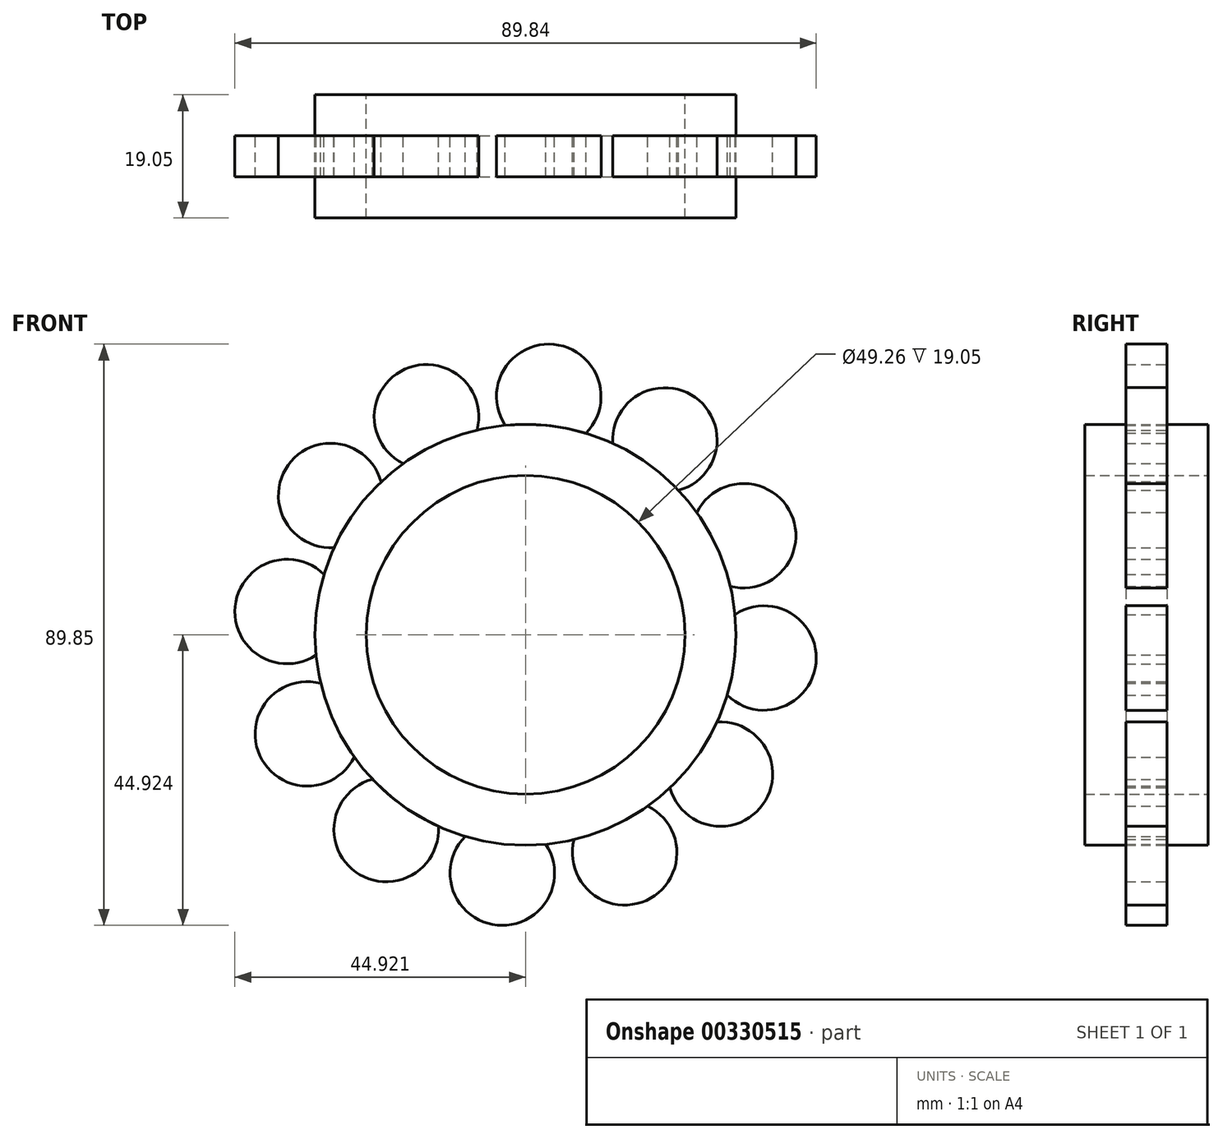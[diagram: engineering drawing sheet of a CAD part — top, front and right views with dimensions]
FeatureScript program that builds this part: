
annotation { "Feature Type Name" : "Feature", "Feature Type Description" : "" }
export const myFeature = defineFeature(function(context is Context, id is Id, definition is map)
    precondition{}
    {
        {
            var Q0;
            Q0=qCreatedBy(makeId("Front.planeOp"),FACE);
            var sketch = newSketch(context, id + "F0", { "sketchPlane" : qUnion([Q0])});
            skCircle(sketch, "E0", {"center": v(-26.17, 22.7) * mm, "radius": 32.53 * mm});
            skSolve(sketch);
        }
        {
            var Q0;
            Q0=sQuery(id+"F0.wireOp",EDGE,"E0");
            extrude(context, id + "F1", {"bodyType" : ToolBodyType.SURFACE, "surfaceEntities" : qUnion([Q0]), "depth" : 6.35 * mm});
        }
        {
            var Q0;
            Q0=qCreatedBy(makeId("Front.planeOp"),FACE);
            var sketch = newSketch(context, id + "F2", { "sketchPlane" : qUnion([Q0])});
            skArc(sketch, "E1", {"start": v(-57.82, 15.2) * mm, "mid": v(-67.23, 4.05) * mm, "end": v(-52.64, 3.8) * mm});
            skCircle(sketch, "E2.0", {"center": v(-26.17, 22.7) * mm, "radius": 32.53 * mm});
            skArc(sketch, "E3.1.0", {"start": v(-49.83, 0.38) * mm, "mid": v(-52.4, -13.98) * mm, "end": v(-39.65, -6.9) * mm});
            skArc(sketch, "E3.2.0", {"start": v(-35.5, -8.46) * mm, "mid": v(-30.54, -22.18) * mm, "end": v(-23.04, -9.67) * mm});
            skArc(sketch, "E3.3.0", {"start": v(-18.66, -8.95) * mm, "mid": v(-7.51, -18.36) * mm, "end": v(-7.27, -3.77) * mm});
            skArc(sketch, "E3.4.0", {"start": v(-3.84, -0.95) * mm, "mid": v(10.52, -3.53) * mm, "end": v(3.44, 9.23) * mm});
            skArc(sketch, "E3.5.0", {"start": v(5, 13.38) * mm, "mid": v(18.72, 18.33) * mm, "end": v(6.2, 25.84) * mm});
            skArc(sketch, "E3.6.0", {"start": v(5.48, 30.21) * mm, "mid": v(14.9, 41.36) * mm, "end": v(0.3, 41.6) * mm});
            skArc(sketch, "E3.7.0", {"start": v(-2.51, 45.03) * mm, "mid": v(0.06, 59.39) * mm, "end": v(-12.7, 52.3) * mm});
            skArc(sketch, "E3.8.0", {"start": v(-16.85, 53.87) * mm, "mid": v(-21.8, 67.59) * mm, "end": v(-29.3, 55.08) * mm});
            skArc(sketch, "E3.9.0", {"start": v(-33.68, 54.35) * mm, "mid": v(-44.82, 63.76) * mm, "end": v(-45.07, 49.18) * mm});
            skArc(sketch, "E3.10.0", {"start": v(-48.5, 46.36) * mm, "mid": v(-62.85, 48.93) * mm, "end": v(-55.77, 36.18) * mm});
            skArc(sketch, "E3.11.0", {"start": v(-57.33, 32.03) * mm, "mid": v(-71.05, 27.08) * mm, "end": v(-58.55, 19.57) * mm});
            skSolve(sketch);
        }
        {
            var Q0;
            {var subQ0=sQuery(id+"F2.wireOp",EDGE,"E3.11.0");Q0=makeQuery(id+"F2.imprint","IMPRINT",FACE,{"disambiguationData":[TD([[makeQuery(id+"F2.imprint","IMPRINT",EDGE,{"derivedFrom":subQ0}),1.0]])]});}
            var Q1;
            {var subQ0=sQuery(id+"F2.wireOp",EDGE,"E3.10.0");Q1=makeQuery(id+"F2.imprint","IMPRINT",FACE,{"disambiguationData":[TD([[makeQuery(id+"F2.imprint","IMPRINT",EDGE,{"derivedFrom":subQ0}),1.0]])]});}
            var Q2;
            {var subQ0=sQuery(id+"F2.wireOp",EDGE,"E3.9.0");Q2=makeQuery(id+"F2.imprint","IMPRINT",FACE,{"disambiguationData":[TD([[makeQuery(id+"F2.imprint","IMPRINT",EDGE,{"derivedFrom":subQ0}),1.0]])]});}
            var Q3;
            {var subQ0=sQuery(id+"F2.wireOp",EDGE,"E3.8.0");Q3=makeQuery(id+"F2.imprint","IMPRINT",FACE,{"disambiguationData":[TD([[makeQuery(id+"F2.imprint","IMPRINT",EDGE,{"derivedFrom":subQ0}),1.0]])]});}
            var Q4;
            {var subQ0=sQuery(id+"F2.wireOp",EDGE,"E3.7.0");Q4=makeQuery(id+"F2.imprint","IMPRINT",FACE,{"disambiguationData":[TD([[makeQuery(id+"F2.imprint","IMPRINT",EDGE,{"derivedFrom":subQ0}),1.0]])]});}
            var Q5;
            {var subQ0=sQuery(id+"F2.wireOp",EDGE,"E3.6.0");Q5=makeQuery(id+"F2.imprint","IMPRINT",FACE,{"disambiguationData":[TD([[makeQuery(id+"F2.imprint","IMPRINT",EDGE,{"derivedFrom":subQ0}),1.0]])]});}
            var Q6;
            {var subQ0=sQuery(id+"F2.wireOp",EDGE,"E3.5.0");Q6=makeQuery(id+"F2.imprint","IMPRINT",FACE,{"disambiguationData":[TD([[makeQuery(id+"F2.imprint","IMPRINT",EDGE,{"derivedFrom":subQ0}),1.0]])]});}
            var Q7;
            {var subQ0=sQuery(id+"F2.wireOp",EDGE,"E3.4.0");Q7=makeQuery(id+"F2.imprint","IMPRINT",FACE,{"disambiguationData":[TD([[makeQuery(id+"F2.imprint","IMPRINT",EDGE,{"derivedFrom":subQ0}),1.0]])]});}
            var Q8;
            {var subQ0=sQuery(id+"F2.wireOp",EDGE,"E3.2.0");Q8=makeQuery(id+"F2.imprint","IMPRINT",FACE,{"disambiguationData":[TD([[makeQuery(id+"F2.imprint","IMPRINT",EDGE,{"derivedFrom":subQ0}),1.0]])]});}
            var Q9;
            {var subQ0=sQuery(id+"F2.wireOp",EDGE,"E3.3.0");Q9=makeQuery(id+"F2.imprint","IMPRINT",FACE,{"disambiguationData":[TD([[makeQuery(id+"F2.imprint","IMPRINT",EDGE,{"derivedFrom":subQ0}),1.0]])]});}
            var Q10;
            {var subQ0=sQuery(id+"F2.wireOp",EDGE,"E3.1.0");Q10=makeQuery(id+"F2.imprint","IMPRINT",FACE,{"disambiguationData":[TD([[makeQuery(id+"F2.imprint","IMPRINT",EDGE,{"derivedFrom":subQ0}),1.0]])]});}
            var Q11;
            {var subQ0=sQuery(id+"F2.wireOp",EDGE,"E1");Q11=makeQuery(id+"F2.imprint","IMPRINT",FACE,{"disambiguationData":[TD([[makeQuery(id+"F2.imprint","IMPRINT",EDGE,{"derivedFrom":subQ0}),1.0]])]});}
            extrude(context, id + "F3", {"entities" : qUnion([Q0, Q1, Q2, Q3, Q4, Q5, Q6, Q7, Q8, Q9, Q10, Q11]), "depth" : 6.35 * mm});
        }
        {
            var Q0;
            Q0=qCreatedBy(makeId("Front.planeOp"),FACE);
            var sketch = newSketch(context, id + "F4", { "sketchPlane" : qUnion([Q0])});
            skCircle(sketch, "E4", {"center": v(-26.17, 22.7) * mm, "radius": 24.63 * mm});
            skCircle(sketch, "E5.0", {"center": v(-26.17, 22.7) * mm, "radius": 32.53 * mm});
            skSolve(sketch);
        }
        {
            var Q0;
            Q0 = qSketchRegion(id + "F4", true);
            extrude(context, id + "F5", {"entities" : qUnion([Q0]), "depth" : 12.7 * mm, "hasSecondDirection" : true, "secondDirectionOppositeDirection" : true, "secondDirectionDepth" : 6.35 * mm});
        }
    });
